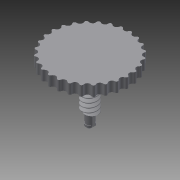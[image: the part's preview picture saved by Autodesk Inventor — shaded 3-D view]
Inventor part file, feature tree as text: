
AUTODESK INVENTOR PART (.ipt)
format: ipt  version: 2015 (Build 190159000, 159)  size: 628,224 bytes
history: native  units: in
note: dims shown in document units (in); Inventor stores cm internally (conversion verified against a paired STEP export)
features: sketch x8, extrude x5, projected_geometry x3, revolve x2, fillet x1, chamfer x1, thread x1, helix x1
ambient origin geometry x8: Origin, YZ Plane, XZ Plane, XY Plane, X Axis, Y Axis, Z Axis, Center Point
bodies: Solid1 (feature_tree), Solid4 (feature_tree)
feature tree (22):
  extrude  "Extrusion1"  Depth=0.4724in TaperAngle=0.0deg
  extrude  "Extrusion2"  Depth=0.315in TaperAngle=0.0deg
  extrude  "Extrusion3"  Depth=0.1181in
  fillet  "Fillet1"  Radius=1.5748in
  extrude  "Extrusion4"  Depth=0.0394in
  extrude  "Extrusion5"  Depth=0.3937in
  chamfer  "Chamfer1"  Distance=0.2008in
  thread  "Thread2"  [1 undecoded]
  revolve  "Revolution5"  Angle=45.0deg
  revolve  "Revolution6"  Angle=60.0deg
  helix  "Coil3"  [1 undecoded]
  sketch  "Sketch1"  dims[d0=0.311in d1=0.4724in d2=0.0in]
  sketch  "Sketch2"  dims[d5=0.4724in d6=0.315in d7=0.0in]
  sketch  "Sketch3"  dims[d8=11.0236in d10=360.0deg d12=0.1181in d13=1.5748in]
  sketch  "Sketch4"  dims[d14=0.1969in d15=0.0in d16=0.0394in]
  projected_geometry  "Projected Loop1"
  sketch  "Sketch5"  dims[d17=0.0591in d18=0.3937in]
  projected_geometry  "Projected Loop4"
  projected_geometry  "Projected Loop5"
  sketch  "Sketch12"  dims[d19=0.1555in d20=0.2008in d21=0.0in d22=0.4331in d23=0.0394in]
  sketch  "Sketch13"  dims[d26=0.0787in d27=0.0in d28=0.0394in d29=0.0787in d30=45.0deg]
  sketch  "Sketch14"  dims[d38=60.0deg d57=60.0deg d69=0.1575in d70=0.0787in d71=0.0787in d72=0.146in d73=0.146in d74=0.0787in d75=0.0079in d76=0.1454in d77=60.0deg d78=0.0133in d79=0.0133in d82=0.0833in d84=60.0deg d86=0.0in d87=0.0in d88=0.0834in d89=0.5997in d90=0.3937in d91=0.0in d92=0.0in d93=0.0in d94=0.0in d95=0.0in]
note: 2 required parameter values undecoded (feature->parameter linkage not recoverable at this tier; creation-order binding heuristic only, values carry confidence <= 0.55)
